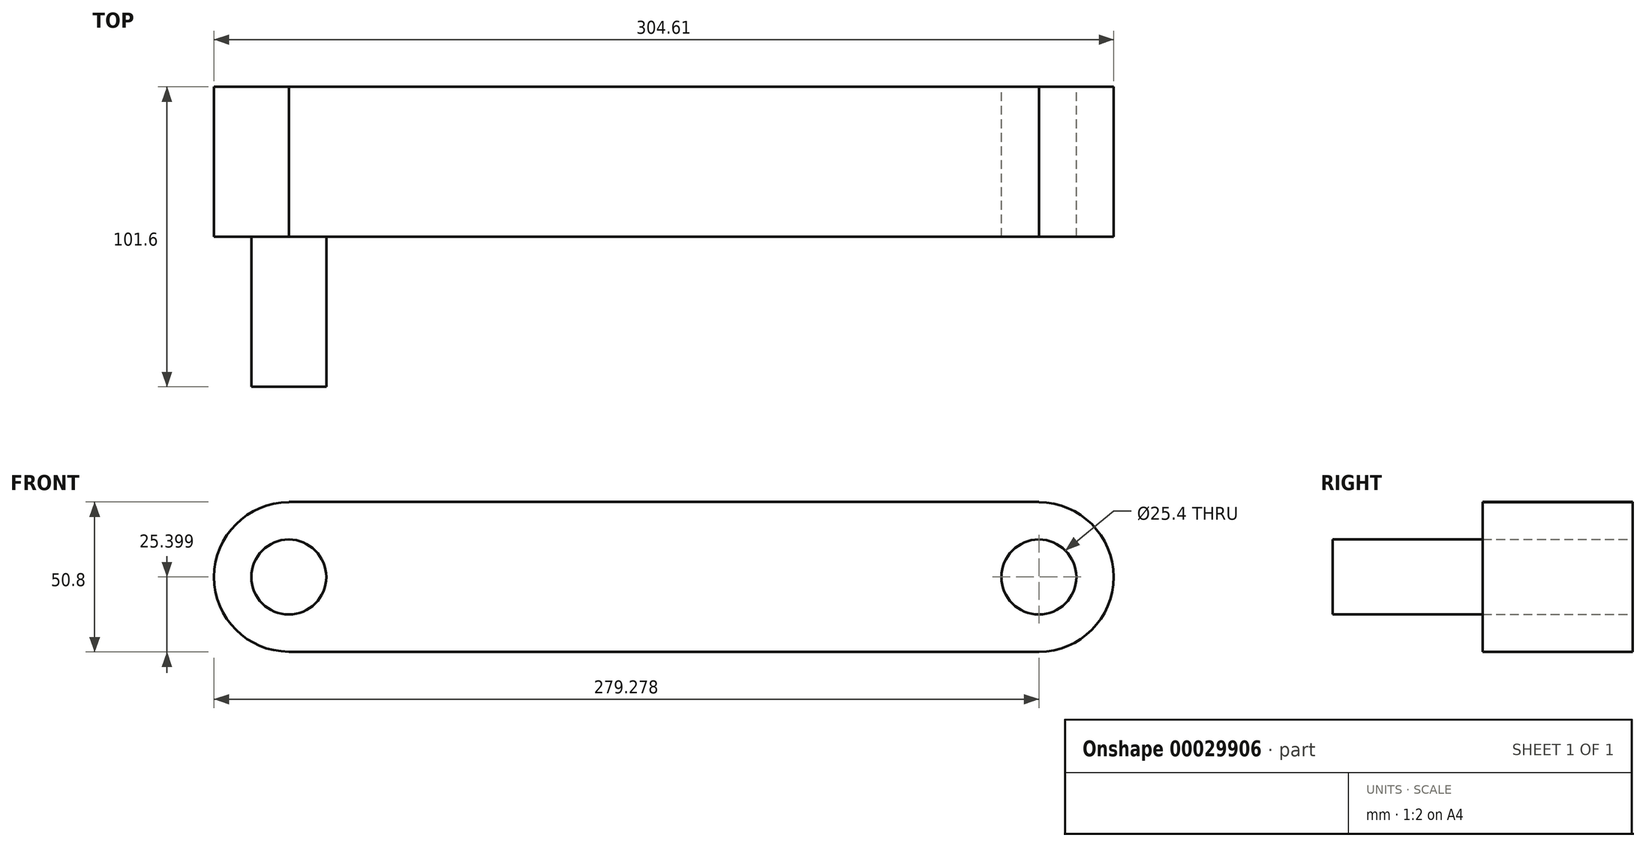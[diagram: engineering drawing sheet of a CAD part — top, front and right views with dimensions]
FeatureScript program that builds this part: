
annotation { "Feature Type Name" : "Feature", "Feature Type Description" : "" }
export const myFeature = defineFeature(function(context is Context, id is Id, definition is map)
    precondition{}
    {
        {
            var Q0;
            Q0=qCreatedBy(makeId("Front.planeOp"),FACE);
            var sketch = newSketch(context, id + "F0", { "sketchPlane" : qUnion([Q0])});
            skLineSegment(sketch, "E0.bottom", {"start": v(-98.84, 26.22) * mm, "end": v(155.16, 26.22) * mm});
            skLineSegment(sketch, "E0.top", {"start": v(-98.84, -24.58) * mm, "end": v(155.16, -24.58) * mm});
            skLineSegment(sketch, "E0.left", {"start": v(-98.84, 26.22) * mm, "end": v(-98.84, 13.52) * mm});
            skLineSegment(sketch, "E0.right", {"start": v(155.16, 26.22) * mm, "end": v(155.16, 13.52) * mm});
            skCircle(sketch, "E1", {"center": v(155.16, 0.82) * mm, "radius": 25.33 * mm});
            skCircle(sketch, "E2", {"center": v(-98.84, 0.82) * mm, "radius": 25.28 * mm});
            skCircle(sketch, "E3", {"center": v(155.16, 0.82) * mm, "radius": 12.7 * mm});
            skLineSegment(sketch, "E4.trimOffspring", {"start": v(155.16, -11.88) * mm, "end": v(155.16, -24.58) * mm});
            skCircle(sketch, "E5", {"center": v(-98.84, 0.82) * mm, "radius": 12.7 * mm});
            skLineSegment(sketch, "E6.trimOffspring", {"start": v(-98.84, -11.88) * mm, "end": v(-98.84, -24.58) * mm});
            skSolve(sketch);
        }
        {
            var Q0;
            Q0=makeQuery(id+"F0.imprint","IMPRINT",FACE,{"disambiguationData":[TD([[makeQuery(id+"F0.imprint","IMPRINT",EDGE,{"derivedFrom":sQuery(id+"F0.wireOp",EDGE,"E0.bottom")}),-1.0]])]});
            extrude(context, id + "F1", {"entities" : qUnion([Q0]), "depth" : 50.8 * mm});
        }
        {
            var Q0;
            Q0=qSketchRegion(id+"F0",true);
            extrude(context, id + "F2", {"entities" : qUnion([Q0]), "operationType" : NewBodyOperationType.ADD, "depth" : 50.8 * mm});
        }
        {
            var Q0;
            Q0=qSketchRegion(id+"F0",true);
            extrude(context, id + "F3", {"entities" : qUnion([Q0]), "operationType" : NewBodyOperationType.ADD, "depth" : 25.4 * mm});
        }
        {
            var Q0;
            {var subQ0=sQuery(id+"F0.wireOp",EDGE,"E5");var subQ2=makeQuery(id+"F0.imprint","INTERSECT",VERTEX,{"derivedFrom":[sQuery(id+"F0.wireOp",EDGE,"E0.left"),subQ0]});Q0=makeQuery(id+"F0.imprint","IMPRINT",FACE,{"disambiguationData":[TD([[makeQuery(id+"F0.imprint","IMPRINT",EDGE,{"disambiguationData":[TD([[subQ2,-1.0]])],"derivedFrom":subQ0}),1.0]])]});}
            extrude(context, id + "F4", {"entities" : qUnion([Q0]), "operationType" : NewBodyOperationType.ADD, "depth" : 101.6 * mm});
        }
    });
